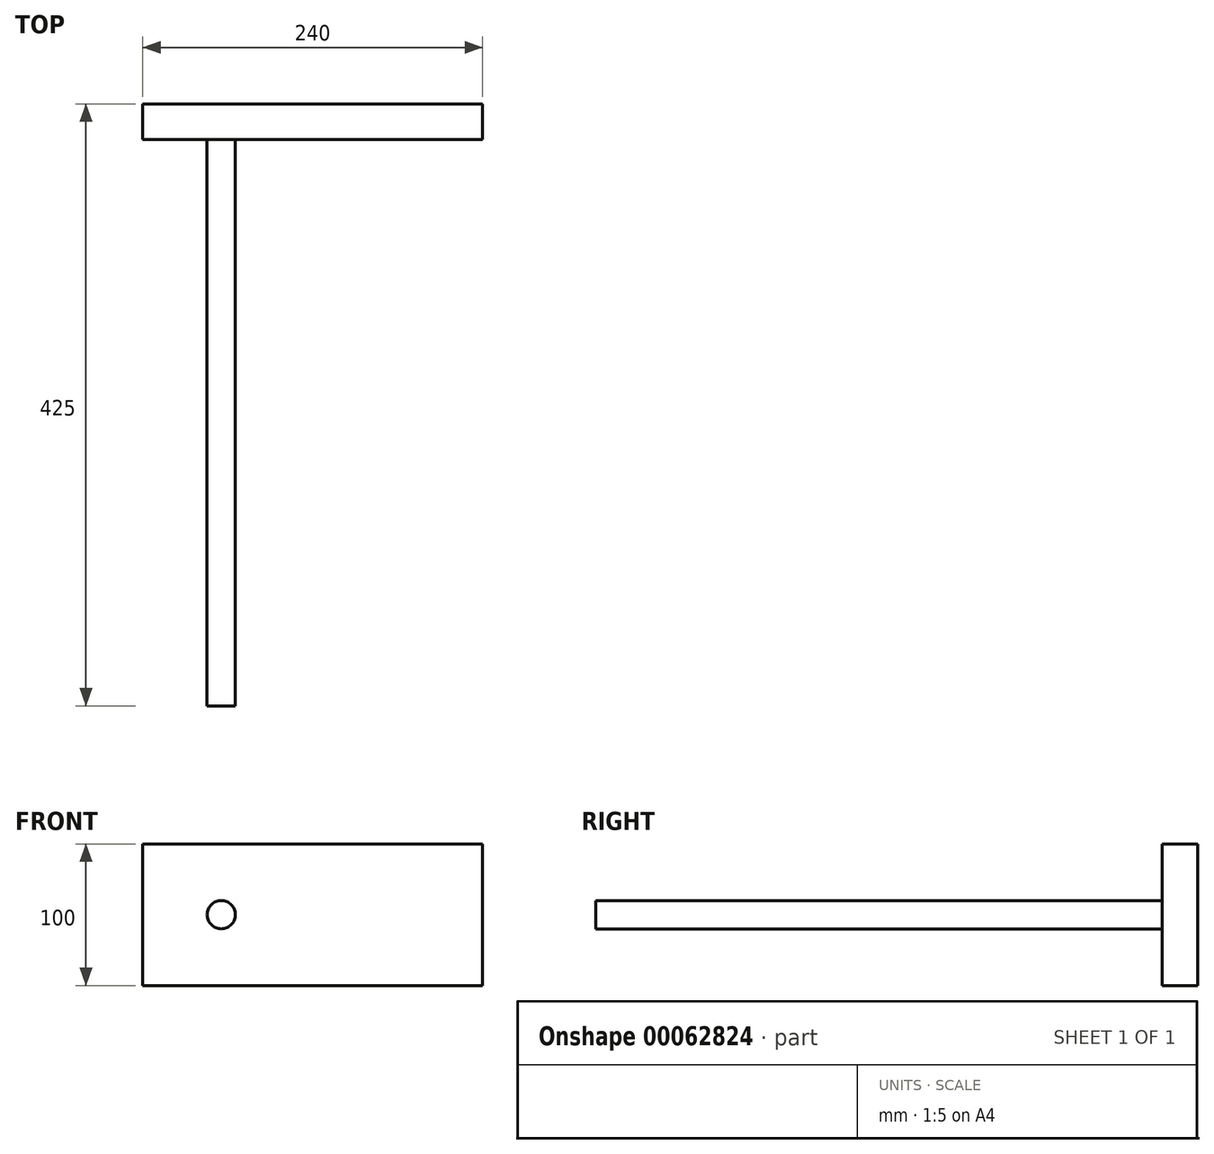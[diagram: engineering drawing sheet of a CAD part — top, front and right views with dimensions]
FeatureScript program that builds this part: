
annotation { "Feature Type Name" : "Feature", "Feature Type Description" : "" }
export const myFeature = defineFeature(function(context is Context, id is Id, definition is map)
    precondition{}
    {
        {
            var Q0;
            Q0=qCreatedBy(makeId("Front.planeOp"),FACE);
            var sketch = newSketch(context, id + "F0", { "sketchPlane" : qUnion([Q0])});
            skLineSegment(sketch, "E0.rect.bottom", {"start": v(120, 50) * mm, "end": v(-120, 50) * mm});
            skLineSegment(sketch, "E0.rect.top", {"start": v(120, -50) * mm, "end": v(-120, -50) * mm});
            skLineSegment(sketch, "E0.rect.left", {"start": v(120, 50) * mm, "end": v(120, -50) * mm});
            skLineSegment(sketch, "E0.rect.right", {"start": v(-120, 50) * mm, "end": v(-120, -50) * mm});
            skPoint(sketch, "E0.rect.middle", {"position": v(0, 0) * mm});
            skSolve(sketch);
        }
        {
            var Q0;
            Q0 = qSketchRegion(id + "F0", true);
            extrude(context, id + "F1", {"entities" : qUnion([Q0]), "depth" : 25 * mm});
        }
        {
            var Q0;
            Q0=makeQuery(id+"F1.opExtrude","CAP_FACE",FACE,{"disambiguationData":[OSD([sQuery(id+"F0.wireOp",EDGE,"E0.rect.bottom"),sQuery(id+"F0.wireOp",EDGE,"E0.rect.top"),sQuery(id+"F0.wireOp",EDGE,"E0.rect.left"),sQuery(id+"F0.wireOp",EDGE,"E0.rect.right")])],"isStart":false});
            var sketch = newSketch(context, id + "F2", { "sketchPlane" : qUnion([Q0])});
            skLineSegment(sketch, "E1", {"start": v(-9.06, 0) * mm, "end": v(-120, 0) * mm, "construction": true});
            skCircle(sketch, "E2", {"center": v(-64.53, 0) * mm, "radius": 10 * mm});
            skSolve(sketch);
        }
        {
            var Q0;
            Q0 = qSketchRegion(id + "F2", true);
            extrude(context, id + "F3", {"entities" : qUnion([Q0]), "operationType" : NewBodyOperationType.ADD, "depth" : 400 * mm});
        }
        {
            var Q0;
            Q0=makeQuery(id+"F3.opExtrude","CAP_FACE",FACE,{"disambiguationData":[OSD([sQuery(id+"F2.wireOp",EDGE,"E2")])],"isStart":false});
            var sketch = newSketch(context, id + "F4", { "sketchPlane" : qUnion([Q0])});
            skLineSegment(sketch, "E3", {"start": v(-54.53, 0) * mm, "end": v(-54.53, 28.13) * mm, "construction": true});
            skSolve(sketch);
        }
    });
